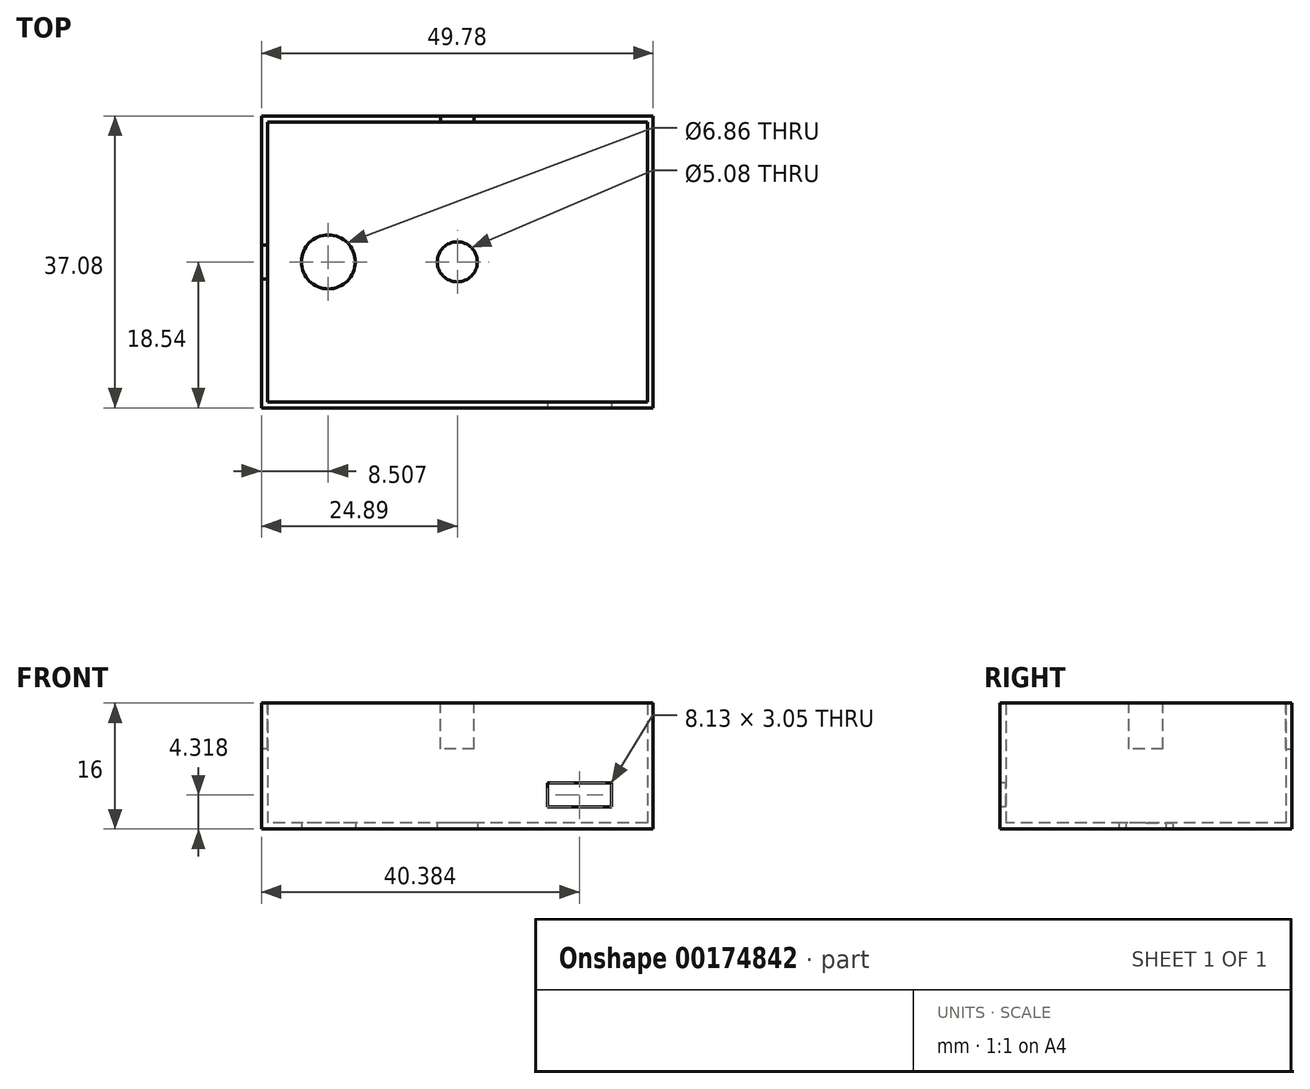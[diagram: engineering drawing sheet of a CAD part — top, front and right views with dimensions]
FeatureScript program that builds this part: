
annotation { "Feature Type Name" : "Feature", "Feature Type Description" : "" }
export const myFeature = defineFeature(function(context is Context, id is Id, definition is map)
    precondition{}
    {
        {
            var Q0;
            Q0=qCreatedBy(makeId("Top.planeOp"),FACE);
            var sketch = newSketch(context, id + "F0", { "sketchPlane" : qUnion([Q0])});
            skLineSegment(sketch, "E0.bottom", {"start": v(24.9, 18.54) * mm, "end": v(-24.9, 18.54) * mm});
            skLineSegment(sketch, "E0.top", {"start": v(24.9, -18.54) * mm, "end": v(-24.9, -18.54) * mm});
            skLineSegment(sketch, "E0.left", {"start": v(24.9, 18.54) * mm, "end": v(24.9, -18.54) * mm});
            skLineSegment(sketch, "E0.right", {"start": v(-24.9, 18.54) * mm, "end": v(-24.9, -18.54) * mm});
            skPoint(sketch, "E0.middle", {"position": v(0, 0) * mm});
            skCircle(sketch, "E1", {"center": v(0, 0) * mm, "radius": 2.92 * mm});
            skLineSegment(sketch, "E2", {"start": v(-24.9, 0) * mm, "end": v(-16.38, 0) * mm});
            skPoint(sketch, "E2.endSnap0", {"position": v(-24.9, 0) * mm});
            skCircle(sketch, "E3", {"center": v(-16.38, 0) * mm, "radius": 3.81 * mm});
            skSolve(sketch);
        }
        {
            var Q0;
            Q0=makeQuery(id+"F0.imprint","IMPRINT",FACE,{"disambiguationData":[TD([[makeQuery(id+"F0.imprint","IMPRINT",EDGE,{"derivedFrom":sQuery(id+"F0.wireOp",EDGE,"E3")}),1.0]])]});
            var Q1;
            {var subQ1=sQuery(id+"F0.wireOp",EDGE,"E0.bottom");Q1=makeQuery(id+"F0.imprint","IMPRINT",FACE,{"disambiguationData":[TD([[makeQuery(id+"F0.imprint","IMPRINT",EDGE,{"derivedFrom":subQ1}),1.0]])]});}
            var Q2;
            Q2=makeQuery(id+"F0.imprint","IMPRINT",FACE,{"disambiguationData":[TD([[makeQuery(id+"F0.imprint","IMPRINT",EDGE,{"derivedFrom":sQuery(id+"F0.wireOp",EDGE,"E1")}),1.0]])]});
            extrude(context, id + "F1", {"entities" : qUnion([Q0, Q1, Q2]), "depth" : 16 * mm});
        }
        {
            var Q0;
            Q0=makeQuery(id+"F1.opExtrude","CAP_FACE",FACE,{"disambiguationData":[OSD([sQuery(id+"F0.wireOp",EDGE,"E0.bottom"),sQuery(id+"F0.wireOp",EDGE,"E0.top"),sQuery(id+"F0.wireOp",EDGE,"E0.left"),sQuery(id+"F0.wireOp",EDGE,"E0.right")])],"isStart":false});
            shell(context, id + "F2", {"entities" : qUnion([Q0]), "thickness" : 0.76 * mm});
        }
        {
            var Q0;
            Q0=sQuery(id+"F0.wireOp",VERTEX,"E2.end");
            var Q1;
            Q1=makeQuery(id+"F1.opExtrude","SWEPT_BODY",BODY,{"disambiguationData":[OSD([sQuery(id+"F0.wireOp",EDGE,"E0.bottom"),sQuery(id+"F0.wireOp",EDGE,"E0.top"),sQuery(id+"F0.wireOp",EDGE,"E0.left"),sQuery(id+"F0.wireOp",EDGE,"E0.right")])]});
            hole(context, id + "F3", {"style" : HoleStyle.SIMPLE, "endStyle" : HoleEndStyle.THROUGH, "oppositeDirection" : true, "holeDiameter" : 6.86 * mm, "locations" : qUnion([Q0]), "scope" : qUnion([Q1]), "isTappedThrough" : true});
        }
        {
            var Q0;
            Q0=sQuery(id+"F0.wireOp",VERTEX,"E0.middle");
            var Q1;
            Q1=makeQuery(id+"F1.opExtrude","SWEPT_BODY",BODY,{"disambiguationData":[OSD([sQuery(id+"F0.wireOp",EDGE,"E0.bottom"),sQuery(id+"F0.wireOp",EDGE,"E0.top"),sQuery(id+"F0.wireOp",EDGE,"E0.left"),sQuery(id+"F0.wireOp",EDGE,"E0.right")])]});
            hole(context, id + "F4", {"style" : HoleStyle.SIMPLE, "endStyle" : HoleEndStyle.THROUGH, "oppositeDirection" : true, "holeDiameter" : 5.08 * mm, "locations" : qUnion([Q0]), "scope" : qUnion([Q1]), "isTappedThrough" : true});
        }
        {
            var Q0;
            Q0=makeQuery(id+"F1.opExtrude","SWEPT_FACE",FACE,{"disambiguationData":[OSD([sQuery(id+"F0.wireOp",EDGE,"E0.top")])]});
            var sketch = newSketch(context, id + "F5", { "sketchPlane" : qUnion([Q0])});
            skLineSegment(sketch, "E4.bottom", {"start": v(24.9, 0) * mm, "end": v(19.56, 0) * mm});
            skLineSegment(sketch, "E4.top", {"start": v(24.9, 2.8) * mm, "end": v(19.56, 2.8) * mm});
            skLineSegment(sketch, "E4.left", {"start": v(24.9, 0) * mm, "end": v(24.9, 2.8) * mm});
            skLineSegment(sketch, "E4.right", {"start": v(19.56, 0) * mm, "end": v(19.56, 2.8) * mm});
            skLineSegment(sketch, "E5.bottom", {"start": v(19.56, 2.8) * mm, "end": v(11.43, 2.8) * mm});
            skLineSegment(sketch, "E5.top", {"start": v(19.56, 5.84) * mm, "end": v(11.43, 5.84) * mm});
            skLineSegment(sketch, "E5.left", {"start": v(19.56, 2.8) * mm, "end": v(19.56, 5.84) * mm});
            skLineSegment(sketch, "E5.right", {"start": v(11.43, 2.8) * mm, "end": v(11.43, 5.84) * mm});
            skSolve(sketch);
        }
        {
            var Q0;
            Q0=makeQuery(id+"F5.imprint","IMPRINT",FACE,{"disambiguationData":[TD([[makeQuery(id+"F5.imprint","IMPRINT",EDGE,{"derivedFrom":sQuery(id+"F5.wireOp",EDGE,"E5.bottom")}),-1.0]])]});
            extrude(context, id + "F6", {"entities" : qUnion([Q0]), "operationType" : NewBodyOperationType.REMOVE, "oppositeDirection" : true, "depth" : 25.4 * mm});
        }
        {
            var Q0;
            Q0=makeQuery(id+"F1.opExtrude","SWEPT_FACE",FACE,{"disambiguationData":[OSD([sQuery(id+"F0.wireOp",EDGE,"E0.bottom")])]});
            var sketch = newSketch(context, id + "F7", { "sketchPlane" : qUnion([Q0])});
            skLineSegment(sketch, "E6", {"start": v(0, 16) * mm, "end": v(0, 13.08) * mm});
            skPoint(sketch, "E6.endSnap0", {"position": v(0, 16) * mm});
            skLineSegment(sketch, "E7.bottom", {"start": v(2.16, 16) * mm, "end": v(-2.16, 16) * mm});
            skLineSegment(sketch, "E7.top", {"start": v(2.16, 10.16) * mm, "end": v(-2.16, 10.16) * mm});
            skLineSegment(sketch, "E7.left", {"start": v(2.16, 16) * mm, "end": v(2.16, 10.16) * mm});
            skLineSegment(sketch, "E7.right", {"start": v(-2.16, 16) * mm, "end": v(-2.16, 10.16) * mm});
            skPoint(sketch, "E7.middle", {"position": v(0, 13.08) * mm});
            skSolve(sketch);
        }
        {
            var Q0;
            Q0 = qSketchRegion(id + "F7", true);
            extrude(context, id + "F8", {"entities" : qUnion([Q0]), "operationType" : NewBodyOperationType.REMOVE, "oppositeDirection" : true, "depth" : 25.4 * mm});
        }
        {
            var Q0;
            Q0=makeQuery(id+"F1.opExtrude","SWEPT_FACE",FACE,{"disambiguationData":[OSD([sQuery(id+"F0.wireOp",EDGE,"E0.right")])]});
            var sketch = newSketch(context, id + "F9", { "sketchPlane" : qUnion([Q0])});
            skLineSegment(sketch, "E8", {"start": v(0, 16) * mm, "end": v(0, 13.08) * mm});
            skPoint(sketch, "E8.endSnap0", {"position": v(0, 16) * mm});
            skLineSegment(sketch, "E9.bottom", {"start": v(2.16, 16) * mm, "end": v(-2.16, 16) * mm});
            skLineSegment(sketch, "E9.top", {"start": v(2.16, 10.16) * mm, "end": v(-2.16, 10.16) * mm});
            skLineSegment(sketch, "E9.left", {"start": v(2.16, 16) * mm, "end": v(2.16, 10.16) * mm});
            skLineSegment(sketch, "E9.right", {"start": v(-2.16, 16) * mm, "end": v(-2.16, 10.16) * mm});
            skPoint(sketch, "E9.middle", {"position": v(0, 13.08) * mm});
            skSolve(sketch);
        }
        {
            var Q0;
            Q0=makeQuery(id+"F9.imprint","IMPRINT",FACE,{"disambiguationData":[TD([[makeQuery(id+"F9.imprint","IMPRINT",EDGE,{"derivedFrom":sQuery(id+"F9.wireOp",EDGE,"E9.top")}),-1.0]])]});
            extrude(context, id + "F10", {"entities" : qUnion([Q0]), "operationType" : NewBodyOperationType.REMOVE, "oppositeDirection" : true, "depth" : 25.4 * mm});
        }
    });
